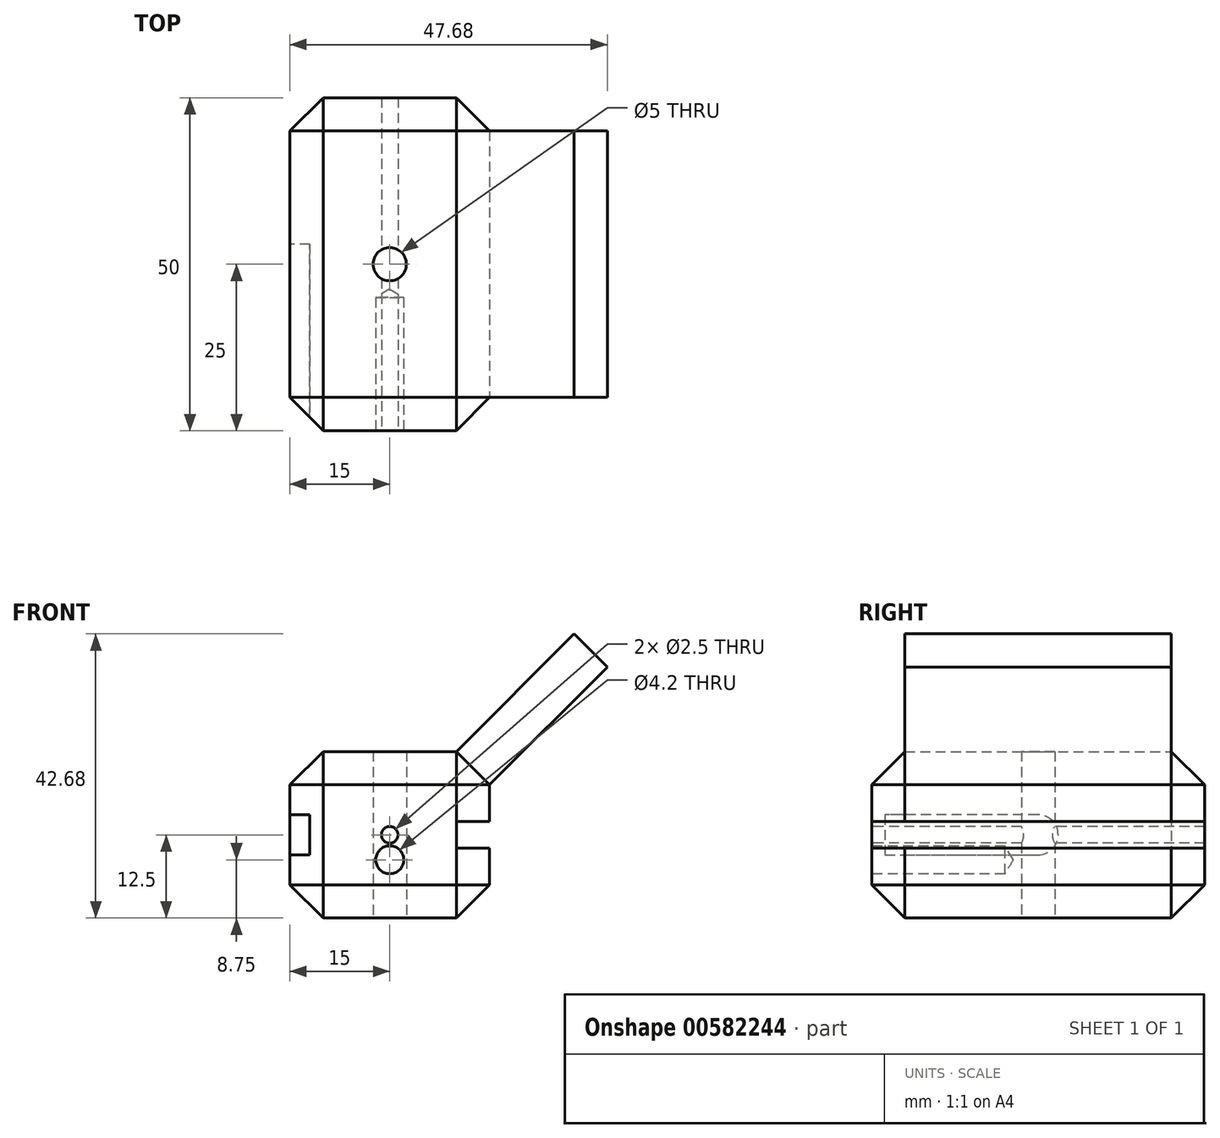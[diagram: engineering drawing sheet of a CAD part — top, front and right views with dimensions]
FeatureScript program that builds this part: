
annotation { "Feature Type Name" : "Feature", "Feature Type Description" : "" }
export const myFeature = defineFeature(function(context is Context, id is Id, definition is map)
    precondition{}
    {
        {
            var Q0;
            Q0=qCreatedBy(makeId("Top.planeOp"),FACE);
            var sketch = newSketch(context, id + "F0", { "sketchPlane" : qUnion([Q0])});
            skLineSegment(sketch, "E0.bottom", {"start": v(0, 0) * mm, "end": v(30, 0) * mm});
            skLineSegment(sketch, "E0.top", {"start": v(0, 50) * mm, "end": v(30, 50) * mm});
            skLineSegment(sketch, "E0.left", {"start": v(0, 0) * mm, "end": v(0, 50) * mm});
            skLineSegment(sketch, "E0.right", {"start": v(30, 0) * mm, "end": v(30, 50) * mm});
            skCircle(sketch, "E1", {"center": v(15, 25) * mm, "radius": 2.5 * mm});
            skPoint(sketch, "E1.centerSnap0", {"position": v(15, 0) * mm});
            skPoint(sketch, "E1.centerSnap1", {"position": v(0, 25) * mm});
            skSolve(sketch);
        }
        {
            var Q0;
            Q0=makeQuery(id+"F0.imprint","IMPRINT",FACE,{"disambiguationData":[TD([[makeQuery(id+"F0.imprint","IMPRINT",EDGE,{"derivedFrom":sQuery(id+"F0.wireOp",EDGE,"E0.bottom")}),1.0]])]});
            var Q1;
            Q1=sQuery(id+"F0.wireOp",EDGE,"E0.left");
            var Q2;
            Q2=sQuery(id+"F0.wireOp",EDGE,"E0.top");
            var Q3;
            Q3=sQuery(id+"F0.wireOp",EDGE,"E0.right");
            var Q4;
            Q4=sQuery(id+"F0.wireOp",EDGE,"E0.bottom");
            extrude(context, id + "F1", {"entities" : qUnion([Q0]), "surfaceEntities" : qUnion([Q1, Q2, Q3, Q4]), "depth" : 25 * mm, "offsetDistance" : 25 * mm});
        }
        {
            var Q0;
            Q0=makeQuery(id+"F1.opExtrude","CAP_EDGE",EDGE,{"disambiguationData":[OSD([sQuery(id+"F0.wireOp",EDGE,"E0.top")])],"isStart":false});
            var Q1;
            Q1=makeQuery(id+"F1.opExtrude","CAP_EDGE",EDGE,{"disambiguationData":[OSD([sQuery(id+"F0.wireOp",EDGE,"E0.right")])],"isStart":false});
            var Q2;
            Q2=makeQuery(id+"F1.opExtrude","CAP_EDGE",EDGE,{"disambiguationData":[OSD([sQuery(id+"F0.wireOp",EDGE,"E0.bottom")])],"isStart":false});
            var Q3;
            Q3=makeQuery(id+"F1.opExtrude","CAP_EDGE",EDGE,{"disambiguationData":[OSD([sQuery(id+"F0.wireOp",EDGE,"E0.left")])],"isStart":false});
            var Q4;
            Q4=makeQuery(id+"F1.opExtrude","CAP_EDGE",EDGE,{"disambiguationData":[OSD([sQuery(id+"F0.wireOp",EDGE,"E0.right")])],"isStart":true});
            var Q5;
            Q5=makeQuery(id+"F1.opExtrude","CAP_EDGE",EDGE,{"disambiguationData":[OSD([sQuery(id+"F0.wireOp",EDGE,"E0.top")])],"isStart":true});
            var Q6;
            Q6=makeQuery(id+"F1.opExtrude","CAP_EDGE",EDGE,{"disambiguationData":[OSD([sQuery(id+"F0.wireOp",EDGE,"E0.left")])],"isStart":true});
            var Q7;
            Q7=makeQuery(id+"F1.opExtrude","CAP_EDGE",EDGE,{"disambiguationData":[OSD([sQuery(id+"F0.wireOp",EDGE,"E0.bottom")])],"isStart":true});
            var Q8;
            Q8=makeQuery(id+"F1.opExtrude","SWEPT_EDGE",EDGE,{"disambiguationData":[OSD([sQuery(id+"F0.wireOp",EDGE,"E0.bottom"),sQuery(id+"F0.wireOp",EDGE,"E0.left")])]});
            var Q9;
            Q9=makeQuery(id+"F1.opExtrude","SWEPT_EDGE",EDGE,{"disambiguationData":[OSD([sQuery(id+"F0.wireOp",EDGE,"E0.bottom"),sQuery(id+"F0.wireOp",EDGE,"E0.right")])]});
            var Q10;
            Q10=makeQuery(id+"F1.opExtrude","SWEPT_EDGE",EDGE,{"disambiguationData":[OSD([sQuery(id+"F0.wireOp",EDGE,"E0.top"),sQuery(id+"F0.wireOp",EDGE,"E0.right")])]});
            var Q11;
            Q11=makeQuery(id+"F1.opExtrude","SWEPT_EDGE",EDGE,{"disambiguationData":[OSD([sQuery(id+"F0.wireOp",EDGE,"E0.top"),sQuery(id+"F0.wireOp",EDGE,"E0.left")])]});
            chamfer(context, id + "F2", {"entities" : qUnion([Q0, Q1, Q2, Q3, Q4, Q5, Q6, Q7, Q8, Q9, Q10, Q11]), "width" : 5 * mm, "tangentPropagation" : true});
        }
        {
            var Q0;
            Q0=makeQuery(id+"F1.opExtrude","SWEPT_FACE",FACE,{"disambiguationData":[OSD([sQuery(id+"F0.wireOp",EDGE,"E0.bottom")])]});
            var sketch = newSketch(context, id + "F3", { "sketchPlane" : qUnion([Q0])});
            skLineSegment(sketch, "E2", {"start": v(25, 12.5) * mm, "end": v(25, 14.5) * mm});
            skLineSegment(sketch, "E3", {"start": v(25, 14.5) * mm, "end": v(32.32, 14.5) * mm});
            skLineSegment(sketch, "E4", {"start": v(32.32, 14.5) * mm, "end": v(32.32, 10.5) * mm});
            skLineSegment(sketch, "E5", {"start": v(32.32, 10.5) * mm, "end": v(25, 10.5) * mm});
            skLineSegment(sketch, "E6", {"start": v(25, 10.5) * mm, "end": v(25, 12.5) * mm});
            skSolve(sketch);
        }
        {
            var Q0;
            Q0=makeQuery(id+"F3.imprint","IMPRINT",FACE,{"disambiguationData":[TD([[makeQuery(id+"F3.imprint","IMPRINT",EDGE,{"derivedFrom":sQuery(id+"F3.wireOp",EDGE,"E2")}),-1.0]])]});
            extrude(context, id + "F4", {"entities" : qUnion([Q0]), "operationType" : NewBodyOperationType.REMOVE, "oppositeDirection" : true, "depth" : 63.1 * mm, "offsetDistance" : 25 * mm});
        }
        {
            var Q0;
            Q0=makeQuery(id+"F1.opExtrude","SWEPT_FACE",FACE,{"disambiguationData":[OSD([sQuery(id+"F0.wireOp",EDGE,"E0.left")])]});
            var sketch = newSketch(context, id + "F5", { "sketchPlane" : qUnion([Q0])});
            skPoint(sketch, "E7.endSnap0", {"position": v(-5, 12.5) * mm});
            skArc(sketch, "E8", {"start": v(-25, 15.5) * mm, "mid": v(-28, 12.5) * mm, "end": v(-25, 9.5) * mm});
            skPoint(sketch, "E7.start.orphan", {"position": v(-5, 12.5) * mm});
            skLineSegment(sketch, "E9", {"start": v(-25, 15.5) * mm, "end": v(7.28, 15.53) * mm});
            skLineSegment(sketch, "E10", {"start": v(7.28, 15.53) * mm, "end": v(7.28, 9.5) * mm});
            skLineSegment(sketch, "E11", {"start": v(7.28, 9.5) * mm, "end": v(-25, 9.5) * mm});
            skSolve(sketch);
        }
        {
            var Q0;
            {var subQ0=sQuery(id+"F5.wireOp",EDGE,"E8");Q0=makeQuery(id+"F5.imprint","IMPRINT",FACE,{"disambiguationData":[TD([[makeQuery(id+"F5.imprint","IMPRINT",EDGE,{"derivedFrom":subQ0}),1.0]])]});}
            var Q1;
            {var subQ0=sQuery(id+"F5.wireOp",EDGE,"E10");Q1=makeQuery(id+"F5.imprint","IMPRINT",FACE,{"disambiguationData":[TD([[makeQuery(id+"F5.imprint","IMPRINT",EDGE,{"derivedFrom":subQ0}),-1.0]])]});}
            extrude(context, id + "F6", {"entities" : qUnion([Q0, Q1]), "operationType" : NewBodyOperationType.REMOVE, "oppositeDirection" : true, "depth" : 3 * mm, "offsetDistance" : 25 * mm});
        }
        {
            var Q0;
            Q0=makeQuery(id+"F1.opExtrude","SWEPT_FACE",FACE,{"disambiguationData":[OSD([sQuery(id+"F0.wireOp",EDGE,"E0.bottom")])]});
            var sketch = newSketch(context, id + "F7", { "sketchPlane" : qUnion([Q0])});
            skLineSegment(sketch, "E12", {"start": v(5, 5) * mm, "end": v(15, 12.5) * mm});
            skPoint(sketch, "E12.endSnap0", {"position": v(5, 12.5) * mm});
            skPoint(sketch, "E12.endSnap1", {"position": v(15, 5) * mm});
            skLineSegment(sketch, "E13", {"start": v(15, 12.5) * mm, "end": v(15, 5) * mm});
            skPoint(sketch, "E14", {"position": v(15, 8.75) * mm});
            skSolve(sketch);
        }
        {
            var Q0;
            Q0=sQuery(id+"F7.wireOp",VERTEX,"E14");
            var Q1;
            Q1=makeQuery(id+"F1.opExtrude","SWEPT_BODY",BODY,{"disambiguationData":[OSD([sQuery(id+"F0.wireOp",EDGE,"E0.bottom"),sQuery(id+"F0.wireOp",EDGE,"E0.top"),sQuery(id+"F0.wireOp",EDGE,"E0.left"),sQuery(id+"F0.wireOp",EDGE,"E0.right"),sQuery(id+"F0.wireOp",EDGE,"E1")])]});
            hole(context, id + "F8", {"style" : HoleStyle.SIMPLE, "endStyle" : HoleEndStyle.BLIND, "standardTappedOrClearance" : lookupTablePath({ "standard" : "ISO", "engagement" : "75%", "pitch" : "0.8 mm", "size" : "M5", "type" : "Tapped" }), "standardBlindInLast" : lookupTablePath({ "standard" : "ISO", "engagement" : "75%", "pitch" : "0.8 mm", "size" : "M5", "type" : "Tapped" }), "holeDiameter" : 4.2 * mm, "majorDiameter" : 5 * mm, "showTappedDepth" : true, "holeDepth" : 20 * mm, "isTappedThrough" : true, "tappedDepth" : 17.6 * mm, "tapClearance" : 3, "locations" : qUnion([Q0]), "scope" : qUnion([Q1])});
        }
        {
            var Q0;
            {var subQ0=sQuery(id+"F0.wireOp",EDGE,"E0.right");Q0=makeQuery(id+"F2.opChamfer","BLEND_FACE",FACE,{"disambiguationData":[OSD([subQ0]),TDD([makeQuery(id+"F1.opExtrude","CAP_EDGE",EDGE,{"disambiguationData":[OSD([subQ0])],"isStart":false})])]});}
            extrude(context, id + "F9", {"entities" : qUnion([Q0]), "depth" : 25 * mm, "offsetDistance" : 25 * mm});
        }
        {
            var Q0;
            Q0=makeQuery(id+"F1.opExtrude","SWEPT_FACE",FACE,{"disambiguationData":[OSD([sQuery(id+"F0.wireOp",EDGE,"E0.bottom")])]});
            var sketch = newSketch(context, id + "F10", { "sketchPlane" : qUnion([Q0])});
            skLineSegment(sketch, "E15", {"start": v(5, 5) * mm, "end": v(25, 20) * mm});
            skLineSegment(sketch, "E16", {"start": v(25, 20) * mm, "end": v(5, 20) * mm});
            skLineSegment(sketch, "E17", {"start": v(5, 20) * mm, "end": v(25, 5) * mm});
            skPoint(sketch, "E18", {"position": v(15, 12.5) * mm});
            skSolve(sketch);
        }
        {
            var Q0;
            Q0=sQuery(id+"F10.wireOp",VERTEX,"E18");
            var Q1;
            Q1=makeQuery(id+"F1.opExtrude","SWEPT_BODY",BODY,{"disambiguationData":[OSD([sQuery(id+"F0.wireOp",EDGE,"E0.bottom"),sQuery(id+"F0.wireOp",EDGE,"E0.top"),sQuery(id+"F0.wireOp",EDGE,"E0.left"),sQuery(id+"F0.wireOp",EDGE,"E0.right"),sQuery(id+"F0.wireOp",EDGE,"E1")])]});
            hole(context, id + "F11", {"style" : HoleStyle.SIMPLE, "endStyle" : HoleEndStyle.THROUGH, "standardTappedOrClearance" : lookupTablePath({ "standard" : "ISO", "engagement" : "75%", "pitch" : "0.5 mm", "size" : "M3", "type" : "Tapped" }), "standardBlindInLast" : lookupTablePath({ "standard" : "ISO", "engagement" : "75%", "pitch" : "0.5 mm", "size" : "M3", "type" : "Tapped" }), "holeDiameter" : 2.5 * mm, "majorDiameter" : 3 * mm, "showTappedDepth" : true, "isTappedThrough" : true, "tappedDepth" : 17.6 * mm, "tapClearance" : 3, "locations" : qUnion([Q0]), "scope" : qUnion([Q1])});
        }
    });
